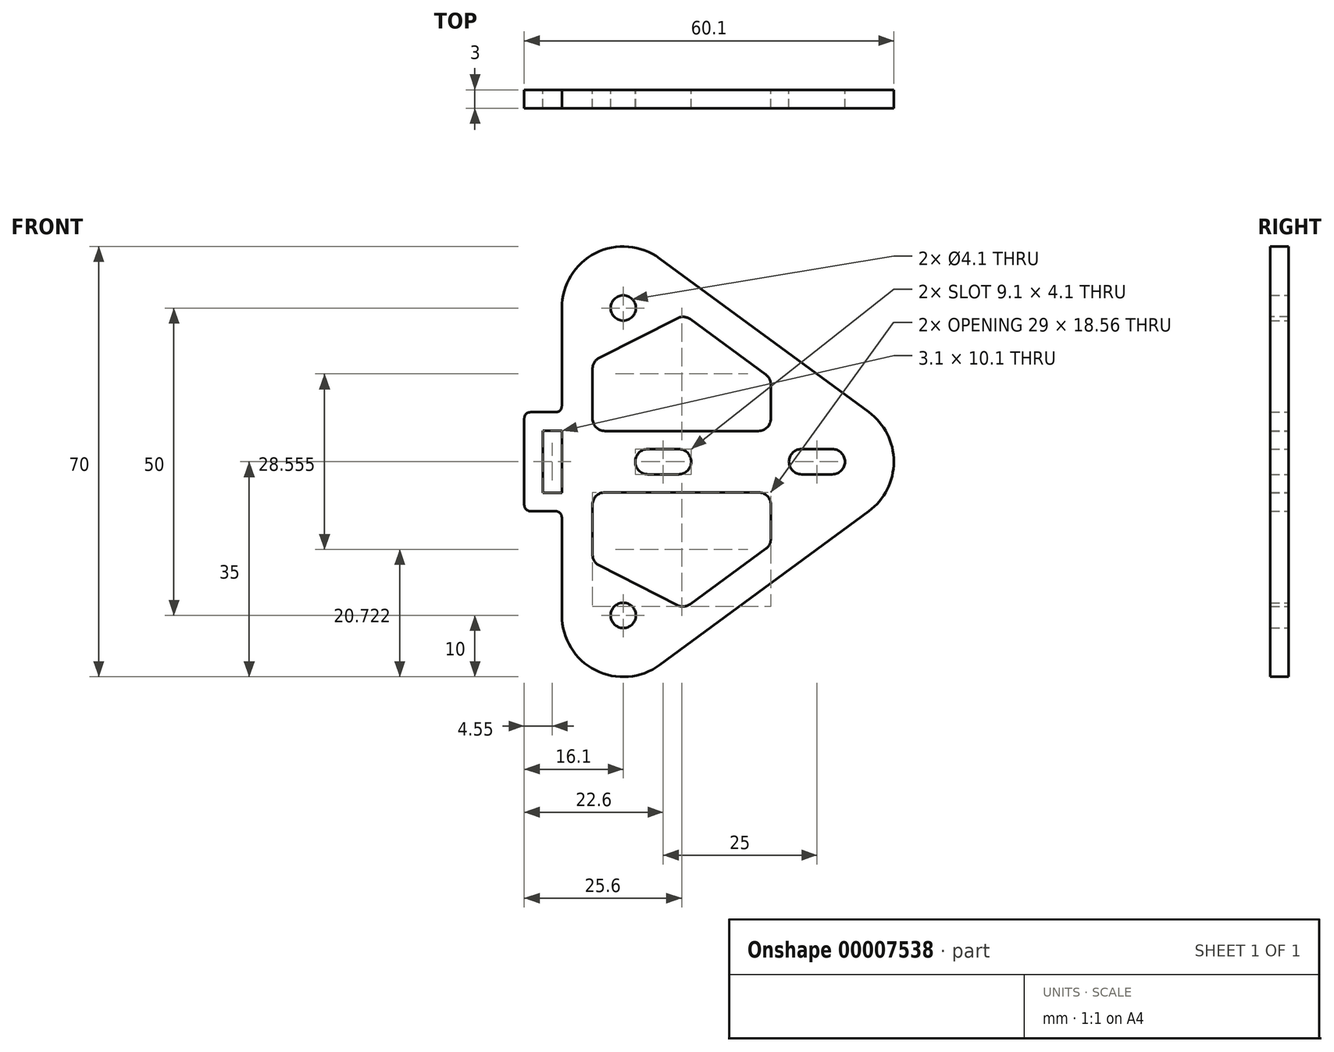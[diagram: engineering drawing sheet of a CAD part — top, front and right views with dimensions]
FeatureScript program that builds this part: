
annotation { "Feature Type Name" : "Feature", "Feature Type Description" : "" }
export const myFeature = defineFeature(function(context is Context, id is Id, definition is map)
    precondition{}
    {
        {
            var Q0;
            Q0=qCreatedBy(makeId("Front.planeOp"),FACE);
            var sketch = newSketch(context, id + "F0", { "sketchPlane" : qUnion([Q0])});
            skCircle(sketch, "E0", {"center": v(-17, 25) * mm, "radius": 2.05 * mm});
            skCircle(sketch, "E1.0.MirrorC", {"center": v(-17, -25) * mm, "radius": 2.05 * mm});
            skArc(sketch, "E2", {"start": v(17, -2.05) * mm, "mid": v(19.05, 0) * mm, "end": v(17, 2.05) * mm});
            skLineSegment(sketch, "E3", {"start": v(-17, 25) * mm, "end": v(-17, -25) * mm, "construction": true});
            skLineSegment(sketch, "E4", {"start": v(17, 0) * mm, "end": v(-17, 0) * mm, "construction": true});
            skArc(sketch, "E5", {"start": v(-11.08, 33.06) * mm, "mid": v(-21.51, 33.92) * mm, "end": v(-27, 25) * mm});
            skArc(sketch, "E6.0.MirrorC", {"start": v(-11.08, -33.06) * mm, "mid": v(-21.51, -33.92) * mm, "end": v(-27, -25) * mm});
            skArc(sketch, "E7", {"start": v(22.92, -8.06) * mm, "mid": v(27, 0) * mm, "end": v(22.92, 8.06) * mm});
            skLineSegment(sketch, "E8", {"start": v(-11.08, 33.06) * mm, "end": v(22.92, 8.06) * mm});
            skLineSegment(sketch, "E9", {"start": v(-11.08, -33.06) * mm, "end": v(22.92, -8.06) * mm});
            skLineSegment(sketch, "E10", {"start": v(-27, 25) * mm, "end": v(-27, 8.05) * mm});
            skLineSegment(sketch, "E11", {"start": v(-17, 25) * mm, "end": v(-11.08, 33.06) * mm, "construction": true});
            skLineSegment(sketch, "E12", {"start": v(17, 0) * mm, "end": v(22.92, 8.06) * mm, "construction": true});
            skLineSegment(sketch, "E13", {"start": v(-17, -25) * mm, "end": v(-11.08, -33.06) * mm, "construction": true});
            skLineSegment(sketch, "E14", {"start": v(17, 0) * mm, "end": v(22.92, -8.06) * mm, "construction": true});
            skLineSegment(sketch, "E15", {"start": v(-27, 8.05) * mm, "end": v(-33.1, 8.05) * mm});
            skLineSegment(sketch, "E16", {"start": v(-33.1, 8.05) * mm, "end": v(-33.1, 0) * mm});
            skLineSegment(sketch, "E17.0.MirrorCS", {"start": v(-33.1, -8.05) * mm, "end": v(-33.1, 0) * mm});
            skLineSegment(sketch, "E18.0.MirrorCS", {"start": v(-27, -8.05) * mm, "end": v(-33.1, -8.05) * mm});
            skLineSegment(sketch, "E19.trimOffspring", {"start": v(-27, -8.05) * mm, "end": v(-27, -25) * mm});
            skLineSegment(sketch, "E20", {"start": v(-27, 5.05) * mm, "end": v(-27, 0) * mm});
            skLineSegment(sketch, "E21", {"start": v(-27, 5.05) * mm, "end": v(-30.1, 5.05) * mm});
            skLineSegment(sketch, "E22", {"start": v(-30.1, 5.05) * mm, "end": v(-30.1, 0) * mm});
            skLineSegment(sketch, "E23.0.MirrorCS", {"start": v(-30.1, -5.05) * mm, "end": v(-30.1, 0) * mm});
            skLineSegment(sketch, "E24.0.MirrorCS", {"start": v(-27, -5.05) * mm, "end": v(-30.1, -5.05) * mm});
            skLineSegment(sketch, "E25.0.MirrorCS", {"start": v(-27, -5.05) * mm, "end": v(-27, 0) * mm});
            skArc(sketch, "E26", {"start": v(12, 2.05) * mm, "mid": v(9.95, 0) * mm, "end": v(12, -2.05) * mm});
            skLineSegment(sketch, "E27", {"start": v(12, 2.05) * mm, "end": v(17, 2.05) * mm});
            skLineSegment(sketch, "E28", {"start": v(12, -2.05) * mm, "end": v(17, -2.05) * mm});
            skArc(sketch, "E29", {"start": v(-27, -25) * mm, "mid": v(-21.51, -33.92) * mm, "end": v(-11.08, -33.06) * mm});
            skLineSegment(sketch, "E30", {"start": v(-22, 16.34) * mm, "end": v(-22, 5) * mm});
            skLineSegment(sketch, "E31", {"start": v(7, -13.56) * mm, "end": v(-7.06, -23.9) * mm});
            skLineSegment(sketch, "E32", {"start": v(-7.06, 23.9) * mm, "end": v(7, 13.56) * mm});
            skLineSegment(sketch, "E33", {"start": v(-22, 16.34) * mm, "end": v(-7.06, 23.9) * mm});
            skLineSegment(sketch, "E34", {"start": v(-22, -16.34) * mm, "end": v(-7.06, -23.9) * mm});
            skLineSegment(sketch, "E35", {"start": v(7, 5) * mm, "end": v(7, 13.56) * mm});
            skLineSegment(sketch, "E36", {"start": v(7, -5) * mm, "end": v(7, -13.56) * mm});
            skLineSegment(sketch, "E37", {"start": v(-22, 5) * mm, "end": v(7, 5) * mm});
            skLineSegment(sketch, "E38.0.MirrorCS", {"start": v(-22, -5) * mm, "end": v(7, -5) * mm});
            skLineSegment(sketch, "E39.trimOffspring", {"start": v(-22, -5) * mm, "end": v(-22, -16.34) * mm});
            skArc(sketch, "E40", {"start": v(-8, -2.05) * mm, "mid": v(-5.95, 0) * mm, "end": v(-8, 2.05) * mm});
            skArc(sketch, "E41", {"start": v(-13, 2.05) * mm, "mid": v(-15.05, 0) * mm, "end": v(-13, -2.05) * mm});
            skLineSegment(sketch, "E42", {"start": v(-13, 2.05) * mm, "end": v(-8, 2.05) * mm});
            skLineSegment(sketch, "E43", {"start": v(-13, -2.05) * mm, "end": v(-8, -2.05) * mm});
            skPoint(sketch, "E44", {"position": v(27, 0) * mm});
            skSolve(sketch);
        }
        {
            var Q0;
            Q0 = qSketchRegion(id + "F0", true);
            extrude(context, id + "F1", {"entities" : qUnion([Q0]), "depth" : 3 * mm});
        }
        {
            var Q0;
            Q0=makeQuery(id+"F1.opExtrude","SWEPT_EDGE",EDGE,{"disambiguationData":[OSD([sQuery(id+"F0.wireOp",EDGE,"E15"),sQuery(id+"F0.wireOp",EDGE,"E16")])]});
            var Q1;
            Q1=makeQuery(id+"F1.opExtrude","SWEPT_EDGE",EDGE,{"disambiguationData":[OSD([sQuery(id+"F0.wireOp",EDGE,"E17.0.MirrorCS"),sQuery(id+"F0.wireOp",EDGE,"E18.0.MirrorCS")])]});
            var Q2;
            Q2=makeQuery(id+"F1.opExtrude","SWEPT_EDGE",EDGE,{"disambiguationData":[OSD([sQuery(id+"F0.wireOp",EDGE,"E10"),sQuery(id+"F0.wireOp",EDGE,"E15")])]});
            var Q3;
            Q3=makeQuery(id+"F1.opExtrude","SWEPT_EDGE",EDGE,{"disambiguationData":[OSD([sQuery(id+"F0.wireOp",EDGE,"E18.0.MirrorCS"),sQuery(id+"F0.wireOp",EDGE,"E19.trimOffspring")])]});
            fillet(context, id + "F2", {"entities" : qUnion([Q0, Q1, Q2, Q3]), "radius" : 1 * mm, "tangentPropagation" : true, "allowEdgeOverflow" : false});
        }
        {
            var Q0;
            Q0=makeQuery(id+"F1.opExtrude","SWEPT_EDGE",EDGE,{"disambiguationData":[OSD([sQuery(id+"F0.wireOp",EDGE,"E30"),sQuery(id+"F0.wireOp",EDGE,"E33")])]});
            var Q1;
            Q1=makeQuery(id+"F1.opExtrude","SWEPT_EDGE",EDGE,{"disambiguationData":[OSD([sQuery(id+"F0.wireOp",EDGE,"E30"),sQuery(id+"F0.wireOp",EDGE,"E37")])]});
            var Q2;
            Q2=makeQuery(id+"F1.opExtrude","SWEPT_EDGE",EDGE,{"disambiguationData":[OSD([sQuery(id+"F0.wireOp",EDGE,"E32"),sQuery(id+"F0.wireOp",EDGE,"E33")])]});
            var Q3;
            Q3=makeQuery(id+"F1.opExtrude","SWEPT_EDGE",EDGE,{"disambiguationData":[OSD([sQuery(id+"F0.wireOp",EDGE,"E32"),sQuery(id+"F0.wireOp",EDGE,"E35")])]});
            var Q4;
            Q4=makeQuery(id+"F1.opExtrude","SWEPT_EDGE",EDGE,{"disambiguationData":[OSD([sQuery(id+"F0.wireOp",EDGE,"E35"),sQuery(id+"F0.wireOp",EDGE,"E37")])]});
            var Q5;
            Q5=makeQuery(id+"F1.opExtrude","SWEPT_EDGE",EDGE,{"disambiguationData":[OSD([sQuery(id+"F0.wireOp",EDGE,"E34"),sQuery(id+"F0.wireOp",EDGE,"E39.trimOffspring")])]});
            var Q6;
            Q6=makeQuery(id+"F1.opExtrude","SWEPT_EDGE",EDGE,{"disambiguationData":[OSD([sQuery(id+"F0.wireOp",EDGE,"E31"),sQuery(id+"F0.wireOp",EDGE,"E34")])]});
            var Q7;
            Q7=makeQuery(id+"F1.opExtrude","SWEPT_EDGE",EDGE,{"disambiguationData":[OSD([sQuery(id+"F0.wireOp",EDGE,"E38.0.MirrorCS"),sQuery(id+"F0.wireOp",EDGE,"E39.trimOffspring")])]});
            var Q8;
            Q8=makeQuery(id+"F1.opExtrude","SWEPT_EDGE",EDGE,{"disambiguationData":[OSD([sQuery(id+"F0.wireOp",EDGE,"E36"),sQuery(id+"F0.wireOp",EDGE,"E38.0.MirrorCS")])]});
            var Q9;
            Q9=makeQuery(id+"F1.opExtrude","SWEPT_EDGE",EDGE,{"disambiguationData":[OSD([sQuery(id+"F0.wireOp",EDGE,"E31"),sQuery(id+"F0.wireOp",EDGE,"E36")])]});
            fillet(context, id + "F3", {"entities" : qUnion([Q0, Q1, Q2, Q3, Q4, Q5, Q6, Q7, Q8, Q9]), "radius" : 2 * mm, "tangentPropagation" : true, "allowEdgeOverflow" : false});
        }
    });
